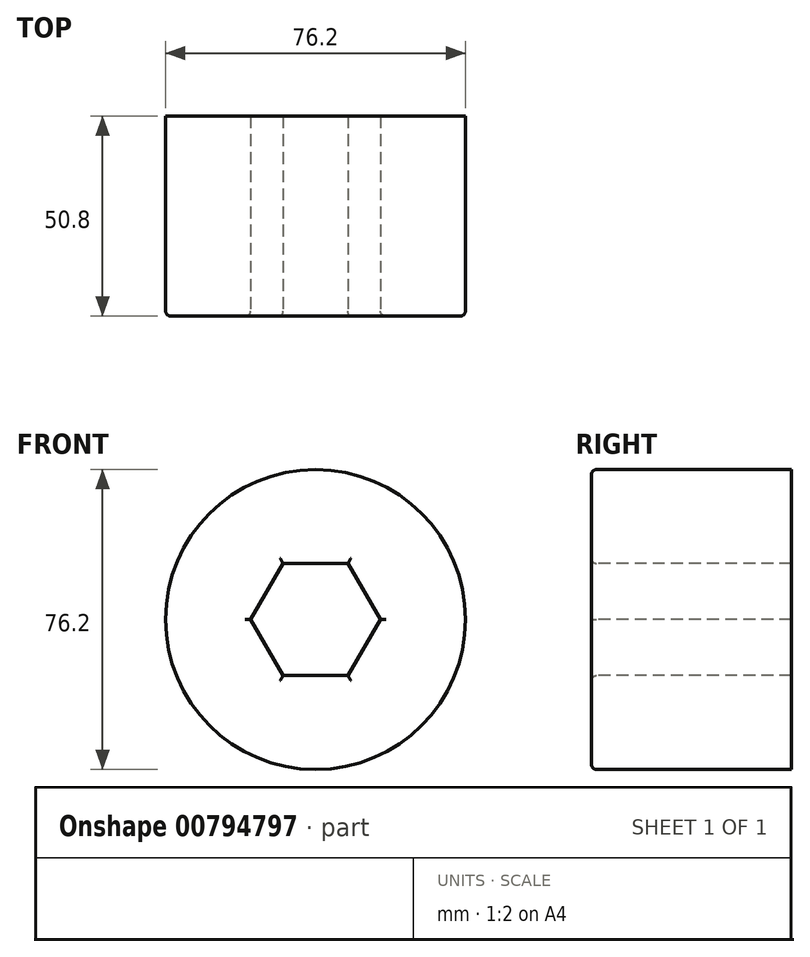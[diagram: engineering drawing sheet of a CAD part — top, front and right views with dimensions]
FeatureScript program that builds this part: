
annotation { "Feature Type Name" : "Feature", "Feature Type Description" : "" }
export const myFeature = defineFeature(function(context is Context, id is Id, definition is map)
    precondition{}
    {
        {
            var Q0;
            Q0=qCreatedBy(makeId("Front.planeOp"),FACE);
            var sketch = newSketch(context, id + "F0", { "sketchPlane" : qUnion([Q0])});
            skCircle(sketch, "E0", {"center": v(0, 0) * mm, "radius": 38.1 * mm});
            skSolve(sketch);
        }
        {
            var Q0;
            Q0=makeQuery(id+"F0.imprint","IMPRINT",FACE,{"disambiguationData":[TD([[makeQuery(id+"F0.imprint","IMPRINT",EDGE,{"derivedFrom":sQuery(id+"F0.wireOp",EDGE,"E0")}),1.0]])]});
            extrude(context, id + "F1", {"entities" : qUnion([Q0]), "depth" : 50.8 * mm, "offsetDistance" : 25.4 * mm});
        }
        {
            var Q0;
            Q0=makeQuery(id+"F1.opExtrude","CAP_FACE",FACE,{"disambiguationData":[OSD([sQuery(id+"F0.wireOp",EDGE,"E0")])],"isStart":false});
            var sketch = newSketch(context, id + "F2", { "sketchPlane" : qUnion([Q0])});
            skCircle(sketch, "E1.cCircle", {"center": v(0, 0) * mm, "radius": 14.26 * mm, "construction": true});
            skLineSegment(sketch, "E1.0", {"start": v(8.23, -14.26) * mm, "end": v(-8.23, -14.26) * mm});
            skLineSegment(sketch, "E1.1", {"start": v(-8.23, -14.26) * mm, "end": v(-16.47, 0) * mm});
            skLineSegment(sketch, "E1.2", {"start": v(-16.47, 0) * mm, "end": v(-8.23, 14.26) * mm});
            skLineSegment(sketch, "E1.3", {"start": v(-8.23, 14.26) * mm, "end": v(8.23, 14.26) * mm});
            skLineSegment(sketch, "E1.4", {"start": v(8.23, 14.26) * mm, "end": v(16.47, 0) * mm});
            skLineSegment(sketch, "E1.5", {"start": v(16.47, 0) * mm, "end": v(8.23, -14.26) * mm});
            skPoint(sketch, "E1.0.midPoint", {"position": v(0, -14.26) * mm});
            skSolve(sketch);
        }
        {
            var Q0;
            Q0=makeQuery(id+"F2.imprint","IMPRINT",FACE,{"disambiguationData":[TD([[makeQuery(id+"F2.imprint","IMPRINT",EDGE,{"derivedFrom":sQuery(id+"F2.wireOp",EDGE,"E1.0")}),-1.0]])]});
            extrude(context, id + "F3", {"entities" : qUnion([Q0]), "operationType" : NewBodyOperationType.REMOVE, "endBound" : BoundingType.THROUGH_ALL, "oppositeDirection" : true, "depth" : 43.18 * mm, "offsetDistance" : 25.4 * mm});
        }
        {
            var Q0;
            Q0=makeQuery(id+"F1.opExtrude","CAP_FACE",FACE,{"disambiguationData":[OSD([sQuery(id+"F0.wireOp",EDGE,"E0")])],"isStart":false});
            fillet(context, id + "F4", {"entities" : qUnion([Q0]), "radius" : 1.27 * mm, "tangentPropagation" : true, "allowEdgeOverflow" : false});
        }
    });
